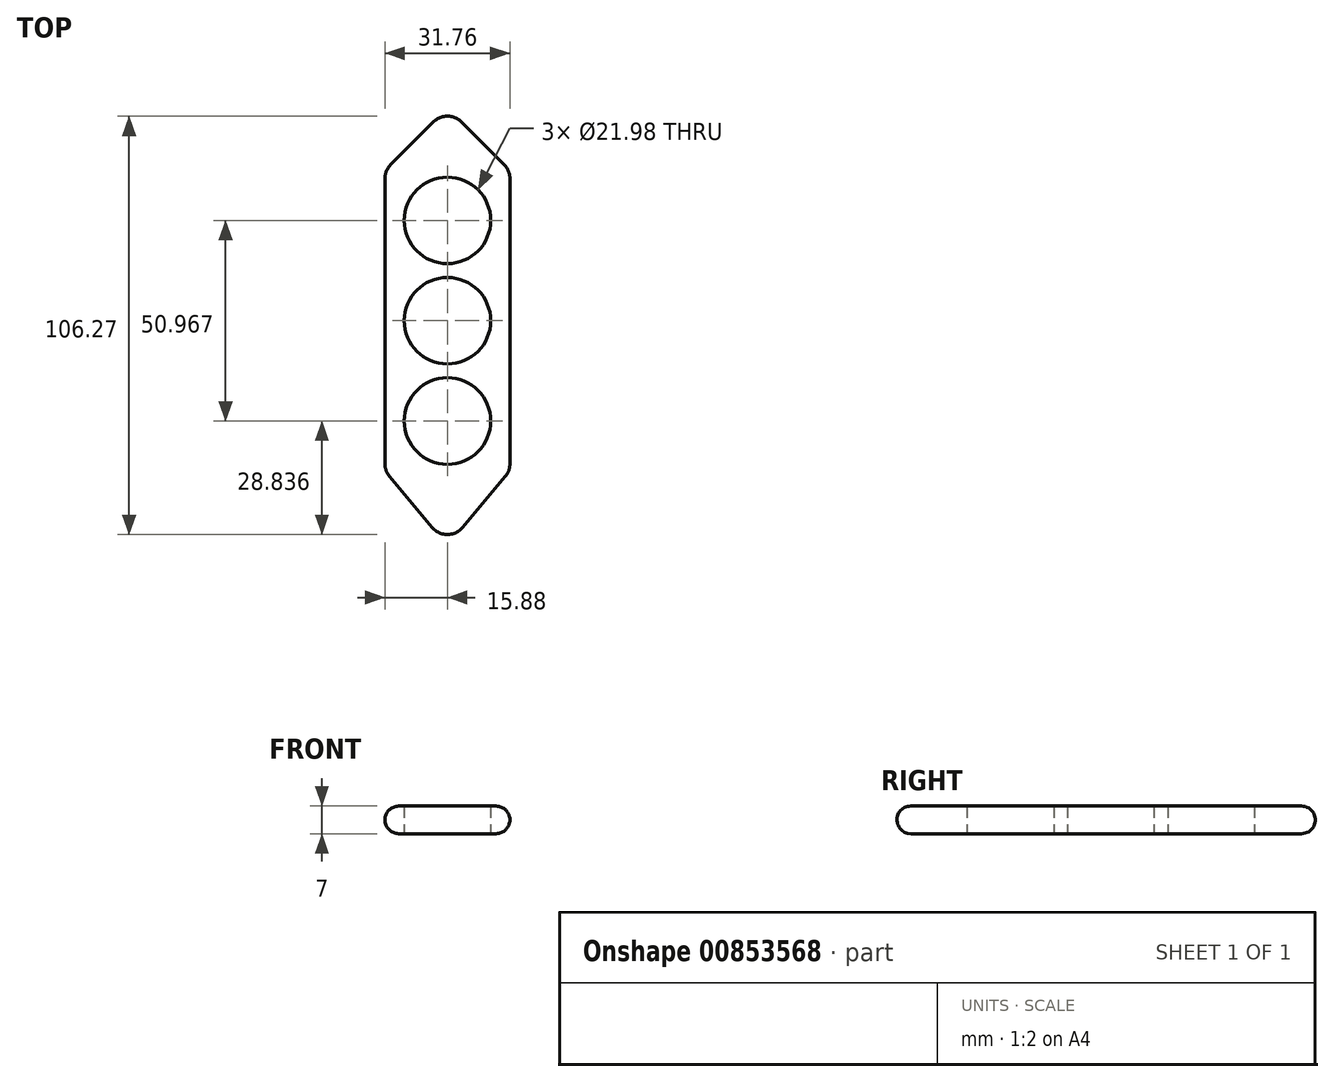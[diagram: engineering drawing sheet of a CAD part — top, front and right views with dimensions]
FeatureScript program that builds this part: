
annotation { "Feature Type Name" : "Feature", "Feature Type Description" : "" }
export const myFeature = defineFeature(function(context is Context, id is Id, definition is map)
    precondition{}
    {
        {
            var Q0;
            Q0=qCreatedBy(makeId("Top.planeOp"),FACE);
            var sketch = newSketch(context, id + "F0", { "sketchPlane" : qUnion([Q0])});
            skCircle(sketch, "E0", {"center": v(0, 0) * mm, "radius": 11 * mm});
            skCircle(sketch, "E1", {"center": v(0, 25.48) * mm, "radius": 11 * mm});
            skCircle(sketch, "E2", {"center": v(0, -25.48) * mm, "radius": 11 * mm});
            skLineSegment(sketch, "E3", {"start": v(0, 25.48) * mm, "end": v(0, -25.48) * mm, "construction": true});
            skLineSegment(sketch, "E4.bottom", {"start": v(-29.85, 57.15) * mm, "end": v(29.85, 57.15) * mm, "construction": true});
            skLineSegment(sketch, "E4.top", {"start": v(-29.85, -57.15) * mm, "end": v(29.85, -57.15) * mm, "construction": true});
            skLineSegment(sketch, "E4.left", {"start": v(-29.84, 57.15) * mm, "end": v(-29.85, -57.15) * mm, "construction": true});
            skLineSegment(sketch, "E4.right", {"start": v(29.85, 57.15) * mm, "end": v(29.84, -57.15) * mm, "construction": true});
            skPoint(sketch, "E5", {"position": v(0, 57.15) * mm});
            skPoint(sketch, "E6", {"position": v(-29.85, 0) * mm});
            skSolve(sketch);
        }
        {
            var Q0;
            Q0=qCreatedBy(makeId("Top.planeOp"),FACE);
            var sketch = newSketch(context, id + "F1", { "sketchPlane" : qUnion([Q0])});
            skCircle(sketch, "E7", {"center": v(0, 25.48) * mm, "radius": 11 * mm});
            skCircle(sketch, "E8", {"center": v(0, 0) * mm, "radius": 11 * mm});
            skCircle(sketch, "E9", {"center": v(0, -25.48) * mm, "radius": 11 * mm});
            skLineSegment(sketch, "E10.bottom", {"start": v(-29.85, 57.15) * mm, "end": v(29.84, 57.15) * mm, "construction": true});
            skLineSegment(sketch, "E10.top", {"start": v(-29.85, -57.15) * mm, "end": v(29.84, -57.15) * mm, "construction": true});
            skLineSegment(sketch, "E10.left", {"start": v(-29.85, 57.15) * mm, "end": v(-29.85, -57.15) * mm, "construction": true});
            skLineSegment(sketch, "E10.right", {"start": v(29.85, 57.15) * mm, "end": v(29.85, -57.15) * mm, "construction": true});
            skPoint(sketch, "E11", {"position": v(-29.85, 0) * mm});
            skPoint(sketch, "E12", {"position": v(0, 57.15) * mm});
            skLineSegment(sketch, "E13", {"start": v(-15.88, 38.18) * mm, "end": v(-15.88, -38.18) * mm});
            skLineSegment(sketch, "E14", {"start": v(15.87, 38.18) * mm, "end": v(15.87, -38.18) * mm});
            skLineSegment(sketch, "E15", {"start": v(-15.88, -38.18) * mm, "end": v(0, -57.15) * mm});
            skLineSegment(sketch, "E16", {"start": v(15.88, -38.18) * mm, "end": v(0, -57.15) * mm});
            skLineSegment(sketch, "E17", {"start": v(-15.88, 38.18) * mm, "end": v(0, 54.06) * mm});
            skLineSegment(sketch, "E18", {"start": v(15.87, 38.18) * mm, "end": v(0, 54.06) * mm});
            skSolve(sketch);
        }
        {
            var Q0;
            Q0 = qSketchRegion(id + "F1", true);
            extrude(context, id + "F2", {"entities" : qUnion([Q0]), "depth" : 7 * mm, "offsetDistance" : 25.4 * mm});
        }
        {
            var Q0;
            Q0=makeQuery(id+"F2.opExtrude","SWEPT_EDGE",EDGE,{"disambiguationData":[OSD([sQuery(id+"F1.wireOp",EDGE,"E13"),sQuery(id+"F1.wireOp",EDGE,"E15")])]});
            var Q1;
            Q1=makeQuery(id+"F2.opExtrude","SWEPT_EDGE",EDGE,{"disambiguationData":[OSD([sQuery(id+"F1.wireOp",EDGE,"E15"),sQuery(id+"F1.wireOp",EDGE,"E16")])]});
            var Q2;
            Q2=makeQuery(id+"F2.opExtrude","SWEPT_EDGE",EDGE,{"disambiguationData":[OSD([sQuery(id+"F1.wireOp",EDGE,"E14"),sQuery(id+"F1.wireOp",EDGE,"E16")])]});
            var Q3;
            Q3=makeQuery(id+"F2.opExtrude","SWEPT_EDGE",EDGE,{"disambiguationData":[OSD([sQuery(id+"F1.wireOp",EDGE,"E14"),sQuery(id+"F1.wireOp",EDGE,"E18")])]});
            var Q4;
            Q4=makeQuery(id+"F2.opExtrude","SWEPT_EDGE",EDGE,{"disambiguationData":[OSD([sQuery(id+"F1.wireOp",EDGE,"E17"),sQuery(id+"F1.wireOp",EDGE,"E18")])]});
            var Q5;
            Q5=makeQuery(id+"F2.opExtrude","SWEPT_EDGE",EDGE,{"disambiguationData":[OSD([sQuery(id+"F1.wireOp",EDGE,"E13"),sQuery(id+"F1.wireOp",EDGE,"E17")])]});
            fillet(context, id + "F3", {"entities" : qUnion([Q0, Q1, Q2, Q3, Q4, Q5]), "radius" : 5.08 * mm, "tangentPropagation" : true, "allowEdgeOverflow" : false});
        }
        {
            var Q0;
            Q0=makeQuery(id+"F2.opExtrude","CAP_EDGE",EDGE,{"disambiguationData":[OSD([sQuery(id+"F1.wireOp",EDGE,"E13")])],"isStart":true});
            var Q1;
            Q1=makeQuery(id+"F2.opExtrude","CAP_EDGE",EDGE,{"disambiguationData":[OSD([sQuery(id+"F1.wireOp",EDGE,"E14")])],"isStart":false});
            fillet(context, id + "F4", {"entities" : qUnion([Q0, Q1]), "radius" : 3.5 * mm, "tangentPropagation" : true, "allowEdgeOverflow" : false});
        }
    });
